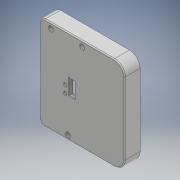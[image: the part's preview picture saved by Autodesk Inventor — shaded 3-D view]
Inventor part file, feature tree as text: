
AUTODESK INVENTOR PART (.ipt)
format: ipt  version: 2017 (Build 210142000, 142)  size: 501,760 bytes
history: native  units: mm
features: sketch x15, extrude x14, projected_geometry x9, fillet x8, chamfer x3, other x1
ambient origin geometry x8: Origin, YZ Plane, XZ Plane, XY Plane, X Axis, Y Axis, Z Axis, Center Point
bodies: Solid1 (feature_tree)
feature tree (50):
  other  "back"
  extrude  "walls"  Depth=87.0mm
  extrude  "string holes"  Depth=4.0mm
  extrude  "PCB pillars"  Depth=15.5mm TaperAngle=0.0deg
  sketch  "Sketch6"  dims[d10=4.0mm d11=10.5mm]
  sketch  "Sketch7"  dims[d12=4.0mm d13=2.0mm d14=0.0mm]
  extrude  "Extrusion5"  Depth=4.0mm
  extrude  "Extrusion6"  Depth=4.0mm
  extrude  "Extrusion7"  Depth=2.0mm TaperAngle=0.0deg
  extrude  "Extrusion8"  Depth=3.5mm
  fillet  "Fillet3"  Radius=91.5mm
  extrude  "room for esp"  Depth=7.0mm
  fillet  "Fillet4"  Radius=3.5mm
  extrude  "inser holes"  Depth=10.0mm
  fillet  "Fillet6"  Radius=9.5mm
  fillet  "Fillet7"  Radius=9.5mm
  chamfer  "Chamfer8"  Distance=3.0mm
  chamfer  "Chamfer9"  Distance=3.0mm
  chamfer  "Chamfer10"  Distance=2.5mm
  fillet  "Fillet11"  Radius=2.0mm
  extrude  "connector hole"  Depth=4.5mm
  fillet  "Fillet13"  Radius=4.5mm
  extrude  "connector"  Depth=0.5mm
  extrude  "buttons hole"  Depth=0.5mm TaperAngle=45.0deg
  extrude  "Extrusion18"  Depth=0.5mm TaperAngle=45.0deg
  extrude  "Extrusion19"  Depth=0.5mm
  fillet  "Fillet14"  Radius=16.0mm
  fillet  "Fillet15"  Radius=5.0mm
  sketch  "Sketch1"  dims[d0=96.0mm d1=87.0mm]
  sketch  "Sketch2"  dims[d2=10.0mm d3=4.0mm]
  projected_geometry  "Projected Loop1"
  sketch  "Sketch3"  dims[d4=1.2mm d5=15.5mm d6=0.0mm]
  sketch  "Sketch5"  dims[d7=1.0mm d8=0.0mm d9=4.0mm]
  projected_geometry  "Projected Loop2"
  projected_geometry  "Projected Loop3"
  sketch  "Sketch8"  dims[d19=5.5mm d22=3.5mm d23=91.5mm]
  sketch  "Sketch9"  dims[d26=10.5mm d27=0.0mm d30=7.0mm d31=3.5mm]
  projected_geometry  "Projected Loop4"
  sketch  "Sketch12"  dims[d34=5.4mm d35=10.0mm d37=9.5mm d38=0.0mm d39=9.5mm d40=0.0mm d41=3.0mm d42=0.0mm d43=3.0mm d44=0.0mm]
  projected_geometry  "Projected Loop6"
  sketch  "Sketch13"  dims[d56=1.0mm]
  projected_geometry  "Projected Loop7"
  sketch  "Sketch14"  dims[d57=1.8mm d58=2.5mm d59=0.0mm d60=2.0mm]
  projected_geometry  "Projected Loop8"
  sketch  "Sketch16"  dims[d77=4.5mm d78=4.5mm d79=4.5mm]
  projected_geometry  "Projected Loop9"
  sketch  "Sketch17"  dims[d80=5.0mm d81=0.0mm d82=0.5mm]
  sketch  "Sketch18"  dims[d83=1.0mm d93=0.5mm d94=2.0mm d95=45.0deg]
  sketch  "Sketch19"  dims[d96=0.5mm d97=2.0mm d98=45.0deg d99=0.5mm d100=2.0mm d101=45.0deg d102=0.5mm d105=16.0mm d106=5.0mm d107=0.0mm d109=0.5mm d110=2.0mm d111=3.0mm d112=0.0mm d113=3.0mm d115=40.0mm d116=48.0mm d117=1.0mm d118=0.0mm d119=5.0mm d120=5.0mm d121=3.0mm d122=0.0mm d123=1.5mm d124=1.5mm d125=1.5mm d126=10.0mm d127=10.0mm d128=0.0mm d129=2.0mm d130=10.5mm d131=33.0mm d132=15.0mm d133=29.5mm d134=6.0mm d135=25.5mm d136=0.5mm d137=15.0mm d138=31.0mm]
  projected_geometry  "Projected Loop10"
